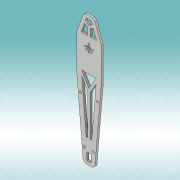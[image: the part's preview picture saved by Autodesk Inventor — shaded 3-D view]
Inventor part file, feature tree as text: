
AUTODESK INVENTOR PART (.ipt)
format: ipt  version: 2019 (Build 230136000, 136)  size: 208,896 bytes
history: native  units: mm
features: extrude x2
ambient origin geometry x8: Origin, YZ Plane, XZ Plane, XY Plane, X Axis, Y Axis, Z Axis, Center Point
bodies: Solid1 (feature_tree)
feature tree (2):
  extrude  "Extrusion1"  Depth=7.0mm
  extrude  "Extrusion2"  Depth=6.0mm
